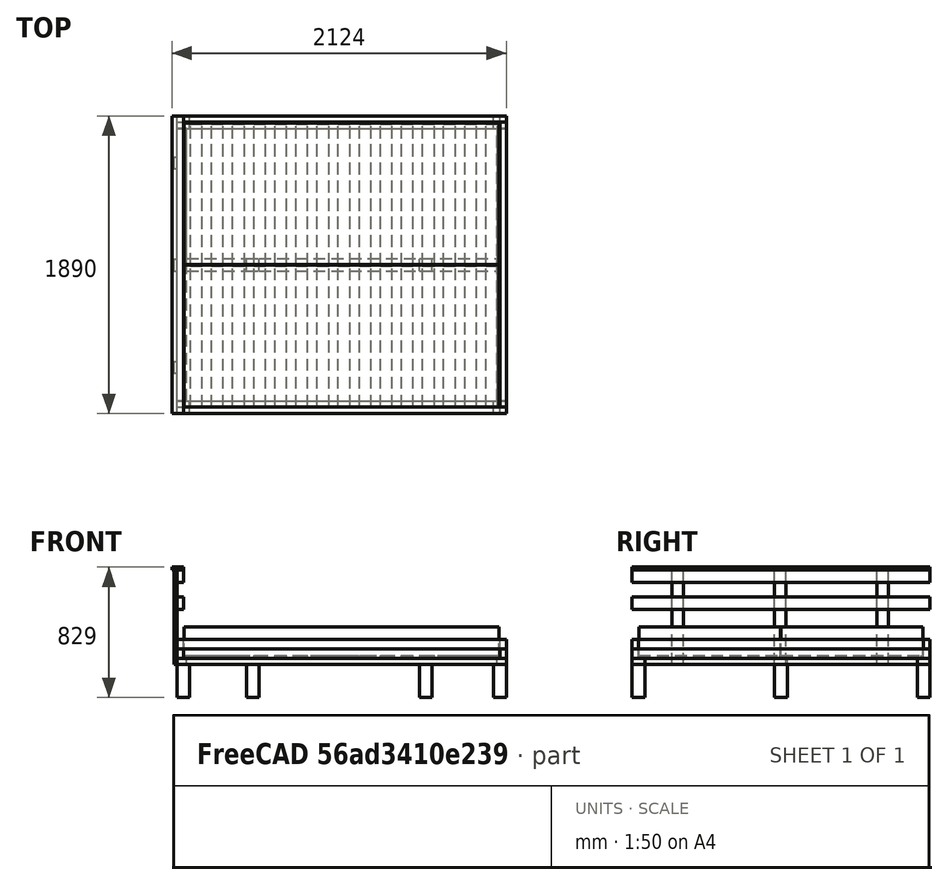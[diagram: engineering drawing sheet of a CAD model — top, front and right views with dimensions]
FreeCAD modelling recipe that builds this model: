
FCSTD DOCUMENT  (FreeCAD 0.18R4 (GitTag))
Label: Bett
License: All rights reserved
LicenseURL: http://en.wikipedia.org/wiki/All_rights_reserved
objects: Part::Box×57, App::DocumentObjectGroup×6
note: 57 computed .brp shape members not serialized (recipe doc carries the construction recipe); baked Part::Feature solids carry a one-line shape summary decoded from their .brp

FEATURE [Part::Box] Box  label="LinksUnten"
  AttacherType = Attacher::AttachEngine3D
  Height = 40
  Length = 2090
  Placement = pos=(-40,-40,0) rot=(0,0,1;0rad)
  Width = 80
FEATURE [Part::Box] Box001  label="RechtsUnten"
  AttacherType = Attacher::AttachEngine3D
  Height = 40
  Length = 2090
  Placement = pos=(-40,1770,0) rot=(0,0,1;0rad)
  Width = 80
FEATURE [Part::Box] Box002  label="VorneUnten"
  AttacherType = Attacher::AttachEngine3D
  Height = 40
  Length = 1730
  Placement = pos=(2050,40,0) rot=(0,0,1;1.5708rad)
  Width = 60
FEATURE [Part::Box] Box003  label="HintenUnten"
  AttacherType = Attacher::AttachEngine3D
  Height = 40
  Length = 1730
  Placement = pos=(20,40,0) rot=(0,0,1;1.5708rad)
  Width = 60
FEATURE [Part::Box] Box004  label="LinksMitte"
  AttacherType = Attacher::AttachEngine3D
  Height = 60
  Length = 2010
  Placement = pos=(0,-40,40) rot=(0,0,1;0rad)
  Width = 40
FEATURE [Part::Box] Box005  label="RechtsMitte"
  AttacherType = Attacher::AttachEngine3D
  Height = 60
  Length = 2010
  Placement = pos=(0,1810,40) rot=(0,0,1;0rad)
  Width = 40
FEATURE [Part::Box] Box006  label="VorneMitte"
  AttacherType = Attacher::AttachEngine3D
  Height = 60
  Length = 1890
  Placement = pos=(2050,-40,40) rot=(0,0,1;1.5708rad)
  Width = 40
FEATURE [Part::Box] Box007  label="HintenMitte"
  AttacherType = Attacher::AttachEngine3D
  Height = 60
  Length = 1890
  Placement = pos=(0,-40,40) rot=(0,0,1;1.5708rad)
  Width = 40
FEATURE [App::DocumentObjectGroup] Gruppe001  label="MittlererTeil"
  Group = -> [Box006,Box007,Box005,Box004]
FEATURE [Part::Box] Box008  label="VorneOben"
  AttacherType = Attacher::AttachEngine3D
  Height = 60
  Length = 1810
  Placement = pos=(2050,0,100) rot=(0,0,1;1.5708rad)
  Width = 40
FEATURE [Part::Box] Box009  label="HintenOben"
  AttacherType = Attacher::AttachEngine3D
  Height = 60
  Length = 1810
  Placement = pos=(0,0,100) rot=(0,0,1;1.5708rad)
  Width = 40
FEATURE [Part::Box] Box010  label="RechtsOben"
  AttacherType = Attacher::AttachEngine3D
  Height = 60
  Length = 2090
  Placement = pos=(-40,1810,100) rot=(0,0,1;0rad)
  Width = 40
FEATURE [Part::Box] Box011  label="LinksOben"
  AttacherType = Attacher::AttachEngine3D
  Height = 60
  Length = 2090
  Placement = pos=(-40,-40,100) rot=(0,0,1;0rad)
  Width = 40
FEATURE [App::DocumentObjectGroup] Gruppe002  label="ObererTeil"
  Group = -> [Box008,Box009,Box010,Box011]
FEATURE [Part::Box] Box012  label="MittelBalken"
  AttacherType = Attacher::AttachEngine3D
  Height = 40
  Length = 1970
  Placement = pos=(20,865,0) rot=(0,0,1;0rad)
  Width = 80
FEATURE [App::DocumentObjectGroup] Gruppe  label="UnterTeil"
  Group = -> [Box,Box001,Box002,Box003,Box012]
FEATURE [Part::Box] Box014  label="HL"
  AttacherType = Attacher::AttachEngine3D
  Height = 210
  Length = 80
  Placement = pos=(-40,-40,-210) rot=(0,0,1;0rad)
  Width = 80
FEATURE [Part::Box] Box015  label="VL"
  AttacherType = Attacher::AttachEngine3D
  Height = 210
  Length = 80
  Placement = pos=(1970,-40,-210) rot=(0,0,1;0rad)
  Width = 80
FEATURE [Part::Box] Box016  label="VR"
  AttacherType = Attacher::AttachEngine3D
  Height = 210
  Length = 80
  Placement = pos=(1970,1770,-210) rot=(0,0,1;0rad)
  Width = 80
FEATURE [Part::Box] Box017  label="HR"
  AttacherType = Attacher::AttachEngine3D
  Height = 210
  Length = 80
  Placement = pos=(-40,1770,-210) rot=(0,0,1;0rad)
  Width = 80
FEATURE [Part::Box] Box018  label="MH"
  AttacherType = Attacher::AttachEngine3D
  Height = 210
  Length = 80
  Placement = pos=(400,865,-210) rot=(0,0,1;0rad)
  Width = 80
FEATURE [Part::Box] Box020  label="MV"
  AttacherType = Attacher::AttachEngine3D
  Height = 210
  Length = 80
  Placement = pos=(1500,865,-210) rot=(0,0,1;0rad)
  Width = 80
FEATURE [App::DocumentObjectGroup] Gruppe003  label="Fuesse"
  Group = -> [Box014,Box015,Box016,Box017,Box018,Box020]
FEATURE [Part::Box] Box021  label="Kopfteil001"
  AttacherType = Attacher::AttachEngine3D
  Height = 80
  Length = 1890
  Placement = pos=(0,-40,350) rot=(0,0,1;1.5708rad)
  Width = 40
FEATURE [Part::Box] Box022  label="KopfteilBrett"
  AttacherType = Attacher::AttachEngine3D
  Height = 19
  Length = 1890
  Placement = pos=(0,-40,600) rot=(0,0,1;1.5708rad)
  Width = 74
FEATURE [Part::Box] Box031  label="Kopfteil002"
  AttacherType = Attacher::AttachEngine3D
  Height = 80
  Length = 1890
  Placement = pos=(0,-40,520) rot=(0,0,1;1.5708rad)
  Width = 40
FEATURE [Part::Box] Box024  label="KopfteilStuetze2"
  AttacherType = Attacher::AttachEngine3D
  Height = 600
  Length = 74
  Placement = pos=(-40,213,0) rot=(0,0,1;1.5708rad)
  Width = 19
FEATURE [Part::Box] Box033  label="KopfteilStuetze1"
  AttacherType = Attacher::AttachEngine3D
  Height = 600
  Length = 74
  Placement = pos=(-40,1513,0) rot=(0,0,1;1.5708rad)
  Width = 20
FEATURE [Part::Box] Box034  label="KopfteilStuetze3"
  AttacherType = Attacher::AttachEngine3D
  Height = 600
  Length = 74
  Placement = pos=(-40,863,0) rot=(0,0,1;1.5708rad)
  Width = 20
FEATURE [App::DocumentObjectGroup] Gruppe004  label="Kopfteil"
  Group = -> [Box021,Box022,Box024,Box031,Box033,Box034]
FEATURE [Part::Box] Box036  label="LatteR"
  AttacherType = Attacher::AttachEngine3D
  Height = 19
  Length = 74
  Placement = pos=(45,902.5,40) rot=(0,0,1;0rad)
  Width = 895
FEATURE [Part::Box] Box037  label="LatteL"
  AttacherType = Attacher::AttachEngine3D
  Height = 19
  Length = 74
  Placement = pos=(45,2.5,40) rot=(0,0,1;0rad)
  Width = 895
FEATURE [Part::Box] Box038  label="LatteR001"
  AttacherType = Attacher::AttachEngine3D
  Height = 19
  Length = 74
  Placement = pos=(179,902.5,40) rot=(0,0,1;0rad)
  Width = 895
FEATURE [Part::Box] Box039  label="LatteL001"
  AttacherType = Attacher::AttachEngine3D
  Height = 19
  Length = 74
  Placement = pos=(179,2.5,40) rot=(0,0,1;0rad)
  Width = 895
FEATURE [Part::Box] Box040  label="LatteR002"
  AttacherType = Attacher::AttachEngine3D
  Height = 19
  Length = 74
  Placement = pos=(313,902.5,40) rot=(0,0,1;0rad)
  Width = 895
FEATURE [Part::Box] Box041  label="LatteL002"
  AttacherType = Attacher::AttachEngine3D
  Height = 19
  Length = 74
  Placement = pos=(313,2.5,40) rot=(0,0,1;0rad)
  Width = 895
FEATURE [Part::Box] Box042  label="LatteR003"
  AttacherType = Attacher::AttachEngine3D
  Height = 19
  Length = 74
  Placement = pos=(447,902.5,40) rot=(0,0,1;0rad)
  Width = 895
FEATURE [Part::Box] Box043  label="LatteL003"
  AttacherType = Attacher::AttachEngine3D
  Height = 19
  Length = 74
  Placement = pos=(447,2.5,40) rot=(0,0,1;0rad)
  Width = 895
FEATURE [Part::Box] Box044  label="LatteR004"
  AttacherType = Attacher::AttachEngine3D
  Height = 19
  Length = 74
  Placement = pos=(581,902.5,40) rot=(0,0,1;0rad)
  Width = 895
FEATURE [Part::Box] Box045  label="LatteL004"
  AttacherType = Attacher::AttachEngine3D
  Height = 19
  Length = 74
  Placement = pos=(581,2.5,40) rot=(0,0,1;0rad)
  Width = 895
FEATURE [Part::Box] Box046  label="LatteR005"
  AttacherType = Attacher::AttachEngine3D
  Height = 19
  Length = 74
  Placement = pos=(715,902.5,40) rot=(0,0,1;0rad)
  Width = 895
FEATURE [Part::Box] Box047  label="LatteL005"
  AttacherType = Attacher::AttachEngine3D
  Height = 19
  Length = 74
  Placement = pos=(715,2.5,40) rot=(0,0,1;0rad)
  Width = 895
FEATURE [Part::Box] Box048  label="LatteR006"
  AttacherType = Attacher::AttachEngine3D
  Height = 19
  Length = 74
  Placement = pos=(849,902.5,40) rot=(0,0,1;0rad)
  Width = 895
FEATURE [Part::Box] Box049  label="LatteL006"
  AttacherType = Attacher::AttachEngine3D
  Height = 19
  Length = 74
  Placement = pos=(849,2.5,40) rot=(0,0,1;0rad)
  Width = 895
FEATURE [Part::Box] Box050  label="LatteR007"
  AttacherType = Attacher::AttachEngine3D
  Height = 19
  Length = 74
  Placement = pos=(983,902.5,40) rot=(0,0,1;0rad)
  Width = 895
FEATURE [Part::Box] Box051  label="LatteL007"
  AttacherType = Attacher::AttachEngine3D
  Height = 19
  Length = 74
  Placement = pos=(983,2.5,40) rot=(0,0,1;0rad)
  Width = 895
FEATURE [Part::Box] Box052  label="LatteR008"
  AttacherType = Attacher::AttachEngine3D
  Height = 19
  Length = 74
  Placement = pos=(1117,902.5,40) rot=(0,0,1;0rad)
  Width = 895
FEATURE [Part::Box] Box053  label="LatteL008"
  AttacherType = Attacher::AttachEngine3D
  Height = 19
  Length = 74
  Placement = pos=(1117,2.5,40) rot=(0,0,1;0rad)
  Width = 895
FEATURE [Part::Box] Box054  label="LatteR009"
  AttacherType = Attacher::AttachEngine3D
  Height = 19
  Length = 74
  Placement = pos=(1251,902.5,40) rot=(0,0,1;0rad)
  Width = 895
FEATURE [Part::Box] Box055  label="LatteL009"
  AttacherType = Attacher::AttachEngine3D
  Height = 19
  Length = 74
  Placement = pos=(1251,2.5,40) rot=(0,0,1;0rad)
  Width = 895
FEATURE [Part::Box] Box056  label="LatteR010"
  AttacherType = Attacher::AttachEngine3D
  Height = 19
  Length = 74
  Placement = pos=(1385,902.5,40) rot=(0,0,1;0rad)
  Width = 895
FEATURE [Part::Box] Box057  label="LatteL010"
  AttacherType = Attacher::AttachEngine3D
  Height = 19
  Length = 74
  Placement = pos=(1385,2.5,40) rot=(0,0,1;0rad)
  Width = 895
FEATURE [Part::Box] Box058  label="LatteR011"
  AttacherType = Attacher::AttachEngine3D
  Height = 19
  Length = 74
  Placement = pos=(1519,902.5,40) rot=(0,0,1;0rad)
  Width = 895
FEATURE [Part::Box] Box059  label="LatteL011"
  AttacherType = Attacher::AttachEngine3D
  Height = 19
  Length = 74
  Placement = pos=(1519,2.5,40) rot=(0,0,1;0rad)
  Width = 895
FEATURE [Part::Box] Box060  label="LatteR012"
  AttacherType = Attacher::AttachEngine3D
  Height = 19
  Length = 74
  Placement = pos=(1653,902.5,40) rot=(0,0,1;0rad)
  Width = 895
FEATURE [Part::Box] Box061  label="LatteL012"
  AttacherType = Attacher::AttachEngine3D
  Height = 19
  Length = 74
  Placement = pos=(1653,2.5,40) rot=(0,0,1;0rad)
  Width = 895
FEATURE [Part::Box] Box062  label="LatteR013"
  AttacherType = Attacher::AttachEngine3D
  Height = 19
  Length = 74
  Placement = pos=(1787,902.5,40) rot=(0,0,1;0rad)
  Width = 895
FEATURE [Part::Box] Box063  label="LatteL013"
  AttacherType = Attacher::AttachEngine3D
  Height = 19
  Length = 74
  Placement = pos=(1787,2.5,40) rot=(0,0,1;0rad)
  Width = 895
FEATURE [Part::Box] Box064  label="LatteR014"
  AttacherType = Attacher::AttachEngine3D
  Height = 19
  Length = 74
  Placement = pos=(1921,902.5,40) rot=(0,0,1;0rad)
  Width = 895
FEATURE [Part::Box] Box065  label="LatteL014"
  AttacherType = Attacher::AttachEngine3D
  Height = 19
  Length = 74
  Placement = pos=(1921,2.5,40) rot=(0,0,1;0rad)
  Width = 895
FEATURE [App::DocumentObjectGroup] Gruppe005  label="Lattenrost"
  Group = -> [Box036,Box037,Box038,Box039,Box040,Box041,Box043,Box042,Box044,Box045,Box047,Box046,Box049,Box048,Box050,Box051,Box052,Box053,Box054,Box055,Box056,Box057,Box059,Box058,Box061,Box060,Box062,Box063,Box065,Box064]
FEATURE [Part::Box] Box066  label="MatratzeLi"
  AttacherType = Attacher::AttachEngine3D
  Height = 180
  Length = 2000
  Placement = pos=(2.5,2.5,59) rot=(0,0,1;0rad)
  Width = 900
FEATURE [Part::Box] Box067  label="MatratzeRe"
  AttacherType = Attacher::AttachEngine3D
  Height = 180
  Length = 2000
  Placement = pos=(2.5,905,59) rot=(0,0,1;0rad)
  Width = 900
